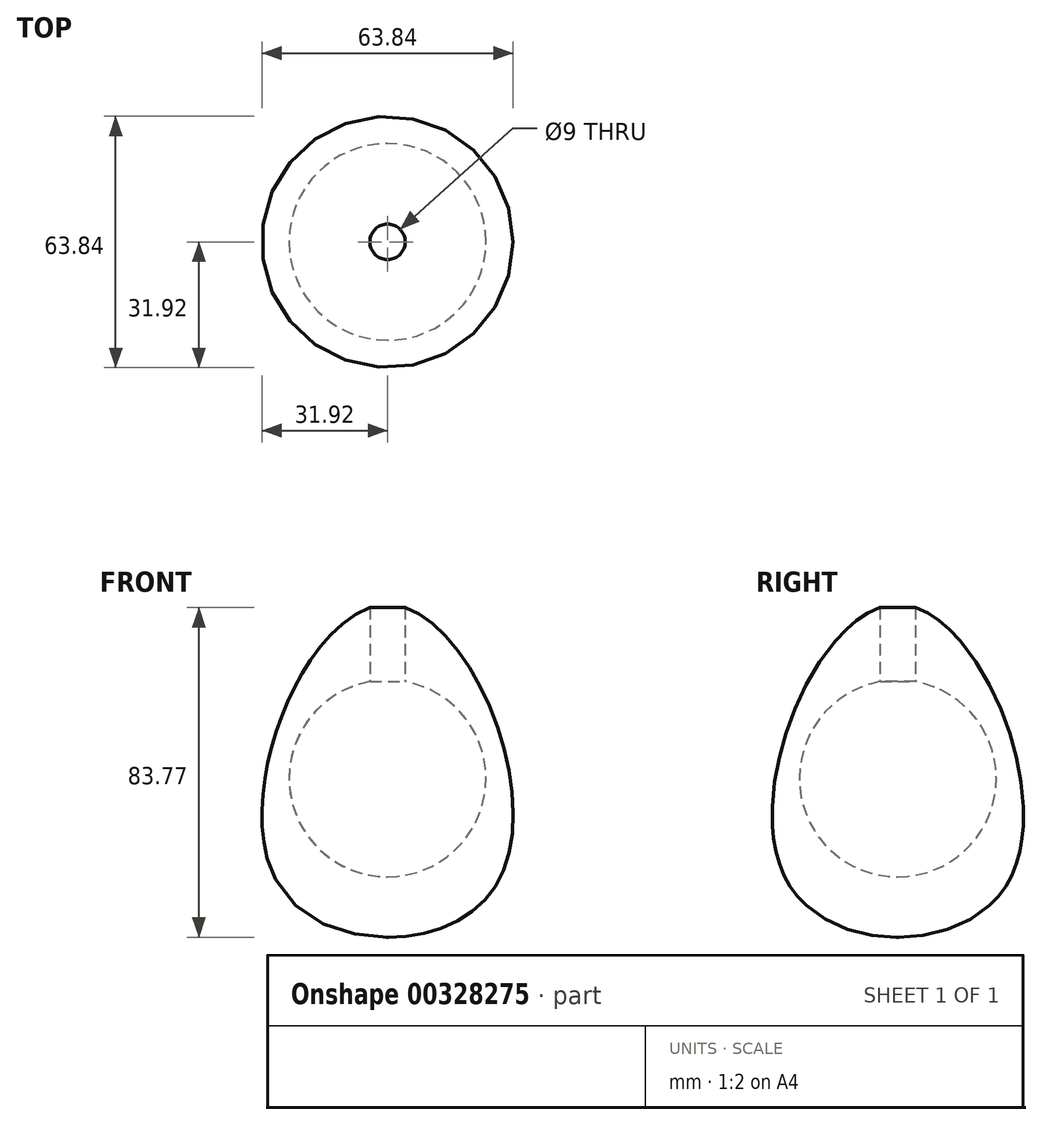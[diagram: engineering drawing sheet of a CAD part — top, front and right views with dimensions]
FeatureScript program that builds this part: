
annotation { "Feature Type Name" : "Feature", "Feature Type Description" : "" }
export const myFeature = defineFeature(function(context is Context, id is Id, definition is map)
    precondition{}
    {
        {
            var Q0;
            Q0=qCreatedBy(makeId("Front.planeOp"),FACE);
            var sketch = newSketch(context, id + "F0", { "sketchPlane" : qUnion([Q0])});
            skFitSpline(sketch, "E0", {"points": [v(-28.47, -25.55) * mm, v(28.07, -26.34) * mm, v(0, 44.2) * mm, v(-28.47, -25.55) * mm]});
            skLineSegment(sketch, "E1", {"start": v(0, 44.2) * mm, "end": v(0, -40.36) * mm});
            skCircle(sketch, "E2", {"center": v(0, 0) * mm, "radius": 25 * mm});
            skSolve(sketch);
        }
        {
            var Q0;
            {var subQ0=sQuery(id+"F0.wireOp",EDGE,"E1");Q0=makeQuery(id+"F0.imprint","IMPRINT",FACE,{"disambiguationData":[TD([[makeQuery(id+"F0.imprint","IMPRINT",EDGE,{"derivedFrom":subQ0}),1.0]])]});}
            var Q1;
            Q1=sQuery(id+"F0.wireOp",EDGE,"E1");
            revolve(context, id + "F1", {"entities" : qUnion([Q0]), "axis" : qUnion([Q1]), "revolveType" : RevolveType.TWO_DIRECTIONS, "oppositeDirection" : true, "angle" : 360 * degree, "angleBack" : 360 * degree});
        }
        {
            var Q0;
            Q0=qCreatedBy(makeId("Top.planeOp"),FACE);
            var sketch = newSketch(context, id + "F2", { "sketchPlane" : qUnion([Q0])});
            skCircle(sketch, "E3", {"center": v(0, 0) * mm, "radius": 4.5 * mm});
            skSolve(sketch);
        }
        {
            var Q0;
            Q0 = qSketchRegion(id + "F2", true);
            extrude(context, id + "F3", {"entities" : qUnion([Q0]), "operationType" : NewBodyOperationType.REMOVE, "depth" : 86.1 * mm});
        }
    });
